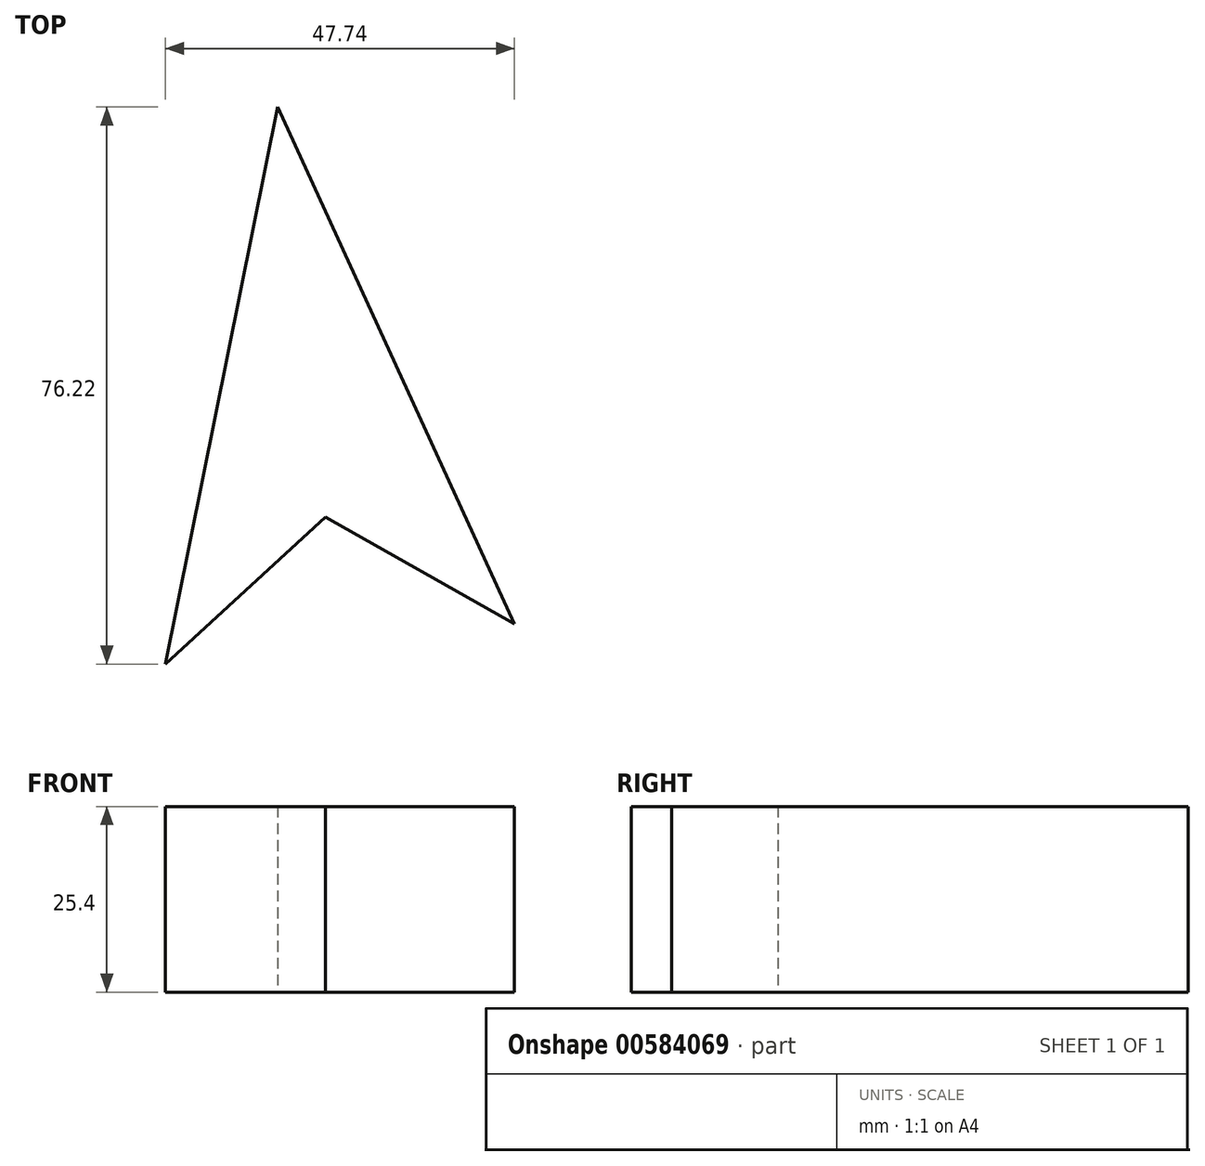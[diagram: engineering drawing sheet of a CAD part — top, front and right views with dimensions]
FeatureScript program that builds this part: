
annotation { "Feature Type Name" : "Feature", "Feature Type Description" : "" }
export const myFeature = defineFeature(function(context is Context, id is Id, definition is map)
    precondition{}
    {
        {
            var Q0;
            Q0=qCreatedBy(makeId("Top.planeOp"),FACE);
            var sketch = newSketch(context, id + "F0", { "sketchPlane" : qUnion([Q0])});
            skCircle(sketch, "E0.cCircle", {"center": v(0, 0) * mm, "radius": 12.63 * mm, "construction": true});
            skLineSegment(sketch, "E0.0", {"start": v(15.3, -3.09) * mm, "end": v(1.8, -15.51) * mm});
            skLineSegment(sketch, "E0.1", {"start": v(1.8, -15.51) * mm, "end": v(-14.2, -6.5) * mm});
            skLineSegment(sketch, "E0.2", {"start": v(-14.2, -6.5) * mm, "end": v(-10.57, 11.5) * mm});
            skLineSegment(sketch, "E0.3", {"start": v(-10.57, 11.5) * mm, "end": v(7.67, 13.6) * mm});
            skLineSegment(sketch, "E0.4", {"start": v(7.67, 13.6) * mm, "end": v(15.3, -3.09) * mm});
            skPoint(sketch, "E0.0.midPoint", {"position": v(8.55, -9.3) * mm});
            skLineSegment(sketch, "E1", {"start": v(-14.2, -6.5) * mm, "end": v(0, 63.88) * mm});
            skLineSegment(sketch, "E2", {"start": v(15.3, -3.09) * mm, "end": v(-9.92, 52.03) * mm});
            skLineSegment(sketch, "E3", {"start": v(-9.92, 52.03) * mm, "end": v(40.55, -58.24) * mm});
            skLineSegment(sketch, "E4", {"start": v(-10.57, 11.5) * mm, "end": v(-23.3, -51.6) * mm});
            skLineSegment(sketch, "E5", {"start": v(-14.2, -6.5) * mm, "end": v(43.25, -38.88) * mm});
            skLineSegment(sketch, "E6", {"start": v(15.3, -3.09) * mm, "end": v(-28, -42.9) * mm});
            skSolve(sketch);
        }
        {
            var Q0;
            {var subQ0=sQuery(id+"F0.wireOp",EDGE,"E5");var subQ1=sQuery(id+"F0.wireOp",EDGE,"E4");var subQ2=makeQuery(id+"F0.imprint","INTERSECT",VERTEX,{"derivedFrom":[subQ1,subQ0]});Q0=makeQuery(id+"F0.imprint","IMPRINT",FACE,{"disambiguationData":[TD([[makeQuery(id+"F0.imprint","IMPRINT",EDGE,{"disambiguationData":[TD([[subQ2,-1.0]])],"derivedFrom":subQ1}),1.0]])]});}
            var Q1;
            {var subQ6=sQuery(id+"F0.wireOp",EDGE,"E0.3");Q1=makeQuery(id+"F0.imprint","IMPRINT",FACE,{"disambiguationData":[TD([[makeQuery(id+"F0.imprint","IMPRINT",EDGE,{"derivedFrom":subQ6}),-1.0]])]});}
            var Q2;
            {var subQ0=sQuery(id+"F0.wireOp",EDGE,"E0.3");Q2=makeQuery(id+"F0.imprint","IMPRINT",FACE,{"disambiguationData":[TD([[makeQuery(id+"F0.imprint","IMPRINT",EDGE,{"derivedFrom":subQ0}),1.0]])]});}
            var Q3;
            {var subQ0=sQuery(id+"F0.wireOp",EDGE,"E6");var subQ1=sQuery(id+"F0.wireOp",EDGE,"E3");var subQ2=makeQuery(id+"F0.imprint","INTERSECT",VERTEX,{"derivedFrom":[subQ1,subQ0]});Q3=makeQuery(id+"F0.imprint","IMPRINT",FACE,{"disambiguationData":[TD([[makeQuery(id+"F0.imprint","IMPRINT",EDGE,{"disambiguationData":[TD([[subQ2,-1.0]])],"derivedFrom":subQ1}),-1.0]])]});}
            extrude(context, id + "F1", {"entities" : qUnion([Q0, Q1, Q2, Q3]), "depth" : 25.4 * mm, "offsetDistance" : 25 * mm});
        }
    });
